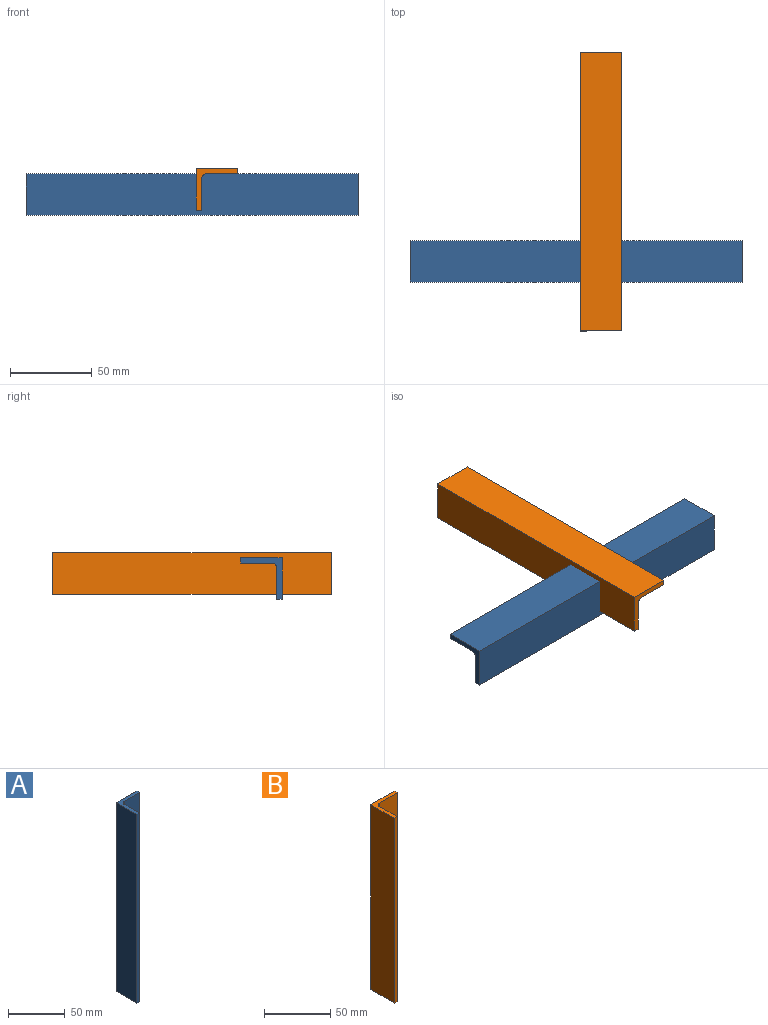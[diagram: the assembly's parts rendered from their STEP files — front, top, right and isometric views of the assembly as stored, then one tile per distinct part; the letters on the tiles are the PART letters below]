
ASSEMBLY  parts=2 mates=1
PART A: 9 faces, bbox 25.4x25.4x203.2 mm
  f0: plane 203.2x3.18mm, normal (1,0,0), area 645.2mm2, adj f1,f5,f6,f7
  f1: plane 203.2x25.4mm, normal (0,1,0), area 5161.3mm2, adj f0,f2,f6,f7
  f2: plane 203.2x25.4mm, normal (-1,0,0), area 5161.3mm2, adj f1,f3,f6,f7
  f3: plane 203.2x3.18mm, normal (0,-1,0), area 645.2mm2, adj f2,f4,f6,f7
  f4: plane 203.2x19.05mm, normal (1,0,0), area 3871mm2, adj f3,f6,f7,f8
  f5: plane 203.2x19.05mm, normal (0,-1,0), area 3871mm2, adj f0,f6,f7,f8
  f6: plane 25.4x25.4mm, normal (0,0,1), area 153.4mm2, adj f0,f1,f2,f3,f4,f5,f8
  f7: plane 25.4x25.4mm, normal (0,0,-1), area 153.4mm2, adj f0,f1,f2,f3,f4,f5,f8
  f8: cylinder r=3.17mm len=203.2mm, axis (0,0,1), area 1013.4mm2, adj f4,f5,f6,f7
PART B: 9 faces, bbox 25.4x25.4x170.2 mm
  f0: plane 170.18x3.18mm, normal (1,0,0), area 540.3mm2, adj f1,f5,f6,f7
  f1: plane 170.18x25.4mm, normal (0,1,0), area 4322.6mm2, adj f0,f2,f6,f7
  f2: plane 170.18x25.4mm, normal (-1,0,0), area 4322.6mm2, adj f1,f3,f6,f7
  f3: plane 170.18x3.18mm, normal (0,-1,0), area 540.3mm2, adj f2,f4,f6,f7
  f4: plane 170.18x19.05mm, normal (1,0,0), area 3241.9mm2, adj f3,f6,f7,f8
  f5: plane 170.18x19.05mm, normal (0,-1,0), area 3241.9mm2, adj f0,f6,f7,f8
  f6: plane 25.4x25.4mm, normal (0,0,1), area 153.4mm2, adj f0,f1,f2,f3,f4,f5,f8
  f7: plane 25.4x25.4mm, normal (0,0,-1), area 153.4mm2, adj f0,f1,f2,f3,f4,f5,f8
  f8: cylinder r=3.17mm len=170.18mm, axis (0,0,1), area 848.7mm2, adj f4,f5,f6,f7
PLACE A rot(axis=(0.71,0,-0.71),180deg) t=(98.96,29.98,-9.94)mm
PLACE B rot(axis=(-0.58,0.58,0.58),120deg) t=(0,0,-6.76)mm
MATE planar A.f2 <-> B.f4  axis (0,0,1) through (-2.64,42.68,-9.94)mm
